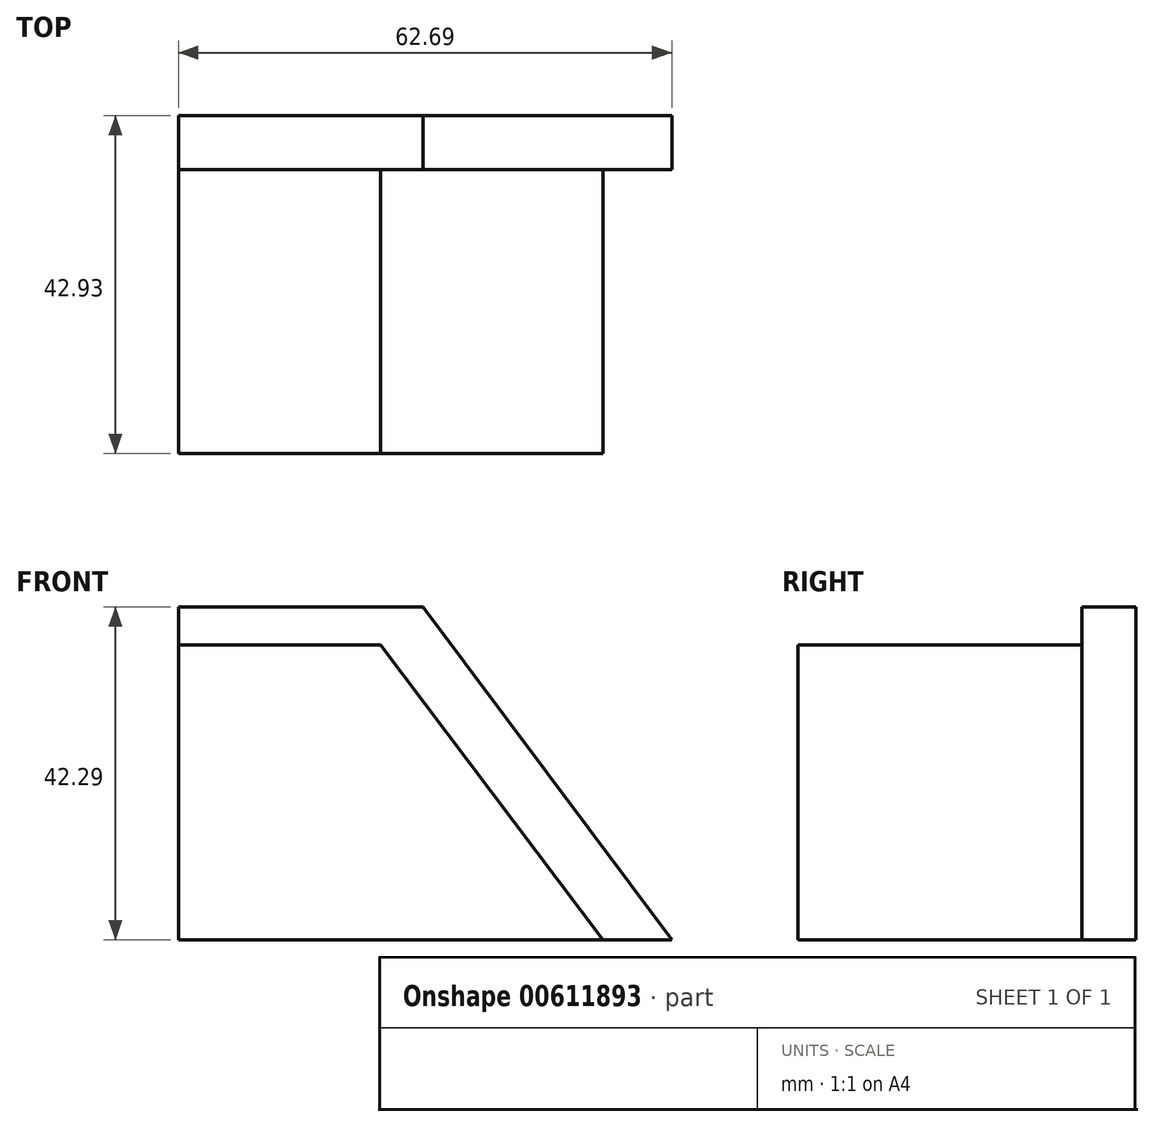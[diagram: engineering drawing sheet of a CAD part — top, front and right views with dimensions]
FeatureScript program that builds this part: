
annotation { "Feature Type Name" : "Feature", "Feature Type Description" : "" }
export const myFeature = defineFeature(function(context is Context, id is Id, definition is map)
    precondition{}
    {
        {
            var Q0;
            Q0=qCreatedBy(makeId("Front.planeOp"),FACE);
            var sketch = newSketch(context, id + "F0", { "sketchPlane" : qUnion([Q0])});
            skLineSegment(sketch, "E0", {"start": v(-25.7, 0) * mm, "end": v(-25.7, 37.48) * mm});
            skLineSegment(sketch, "E1", {"start": v(-25.7, 37.48) * mm, "end": v(0, 37.48) * mm});
            skLineSegment(sketch, "E2", {"start": v(0, 37.48) * mm, "end": v(28.25, 0) * mm});
            skLineSegment(sketch, "E3", {"start": v(28.25, 0) * mm, "end": v(-25.7, 0) * mm});
            skSolve(sketch);
        }
        {
            var Q0;
            Q0 = qSketchRegion(id + "F0", true);
            extrude(context, id + "F1", {"entities" : qUnion([Q0]), "depth" : 36.07 * mm, "offsetDistance" : 25.4 * mm});
        }
        {
            var Q0;
            Q0=makeQuery(id+"F1.opExtrude","CAP_FACE",FACE,{"disambiguationData":[OSD([sQuery(id+"F0.wireOp",EDGE,"E0"),sQuery(id+"F0.wireOp",EDGE,"E1"),sQuery(id+"F0.wireOp",EDGE,"E2"),sQuery(id+"F0.wireOp",EDGE,"E3")])],"isStart":true});
            var sketch = newSketch(context, id + "F2", { "sketchPlane" : qUnion([Q0])});
            skLineSegment(sketch, "E4", {"start": v(25.7, 0) * mm, "end": v(-36.99, 0) * mm});
            skLineSegment(sketch, "E5", {"start": v(-36.99, 0) * mm, "end": v(-5.37, 42.3) * mm});
            skLineSegment(sketch, "E6", {"start": v(-5.37, 42.3) * mm, "end": v(25.7, 42.3) * mm});
            skLineSegment(sketch, "E7", {"start": v(25.7, 42.3) * mm, "end": v(25.7, 0) * mm});
            skSolve(sketch);
        }
        {
            var Q0;
            Q0 = qSketchRegion(id + "F2", true);
            extrude(context, id + "F3", {"entities" : qUnion([Q0]), "operationType" : NewBodyOperationType.ADD, "depth" : 6.86 * mm, "offsetDistance" : 25.4 * mm});
        }
    });
